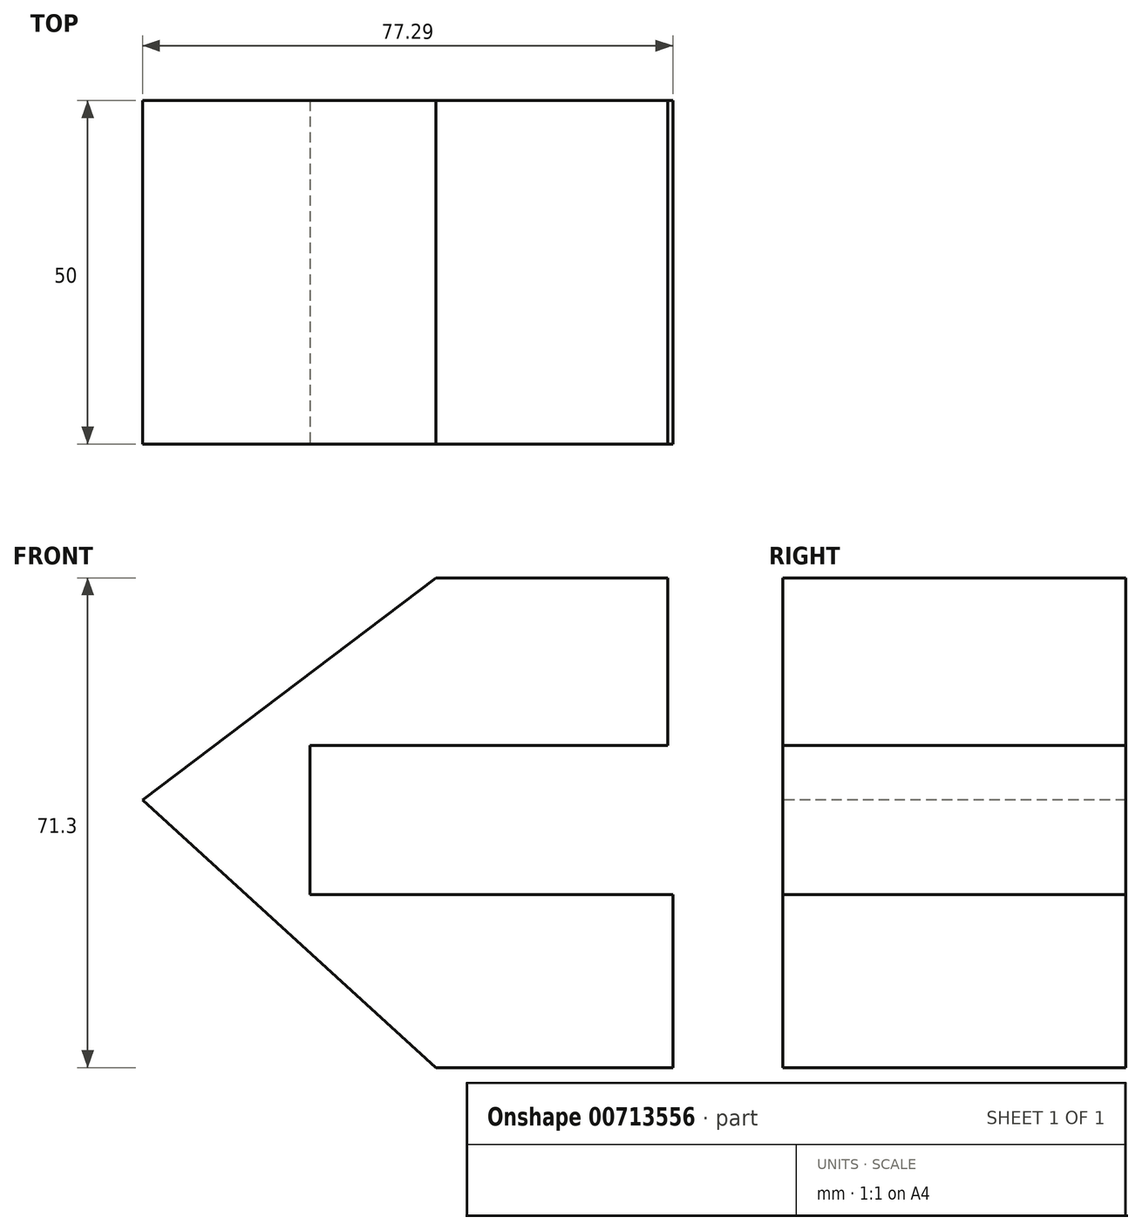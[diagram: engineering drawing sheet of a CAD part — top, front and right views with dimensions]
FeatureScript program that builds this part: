
annotation { "Feature Type Name" : "Feature", "Feature Type Description" : "" }
export const myFeature = defineFeature(function(context is Context, id is Id, definition is map)
    precondition{}
    {
        {
            var Q0;
            Q0=qCreatedBy(makeId("Front.planeOp"),FACE);
            var sketch = newSketch(context, id + "F0", { "sketchPlane" : qUnion([Q0])});
            skLineSegment(sketch, "E0", {"start": v(0, 0) * mm, "end": v(34.52, 0) * mm});
            skLineSegment(sketch, "E1", {"start": v(34.52, 0) * mm, "end": v(34.52, 25.21) * mm});
            skLineSegment(sketch, "E2", {"start": v(34.52, 25.21) * mm, "end": v(-18.35, 25.21) * mm});
            skLineSegment(sketch, "E3", {"start": v(-18.35, 25.21) * mm, "end": v(-18.35, 46.9) * mm});
            skLineSegment(sketch, "E4", {"start": v(-18.35, 46.9) * mm, "end": v(33.77, 46.9) * mm});
            skLineSegment(sketch, "E5", {"start": v(33.77, 46.9) * mm, "end": v(33.77, 71.3) * mm});
            skLineSegment(sketch, "E6", {"start": v(33.77, 71.3) * mm, "end": v(0, 71.3) * mm});
            skLineSegment(sketch, "E7", {"start": v(0, 71.3) * mm, "end": v(-42.77, 38.93) * mm});
            skLineSegment(sketch, "E8", {"start": v(-42.77, 38.93) * mm, "end": v(0, 0) * mm});
            skSolve(sketch);
        }
        {
            var Q0;
            Q0=makeQuery(id+"F0.imprint","IMPRINT",FACE,{"disambiguationData":[TD([[makeQuery(id+"F0.imprint","IMPRINT",EDGE,{"derivedFrom":sQuery(id+"F0.wireOp",EDGE,"E0")}),1.0]])]});
            extrude(context, id + "F1", {"entities" : qUnion([Q0]), "oppositeDirection" : true, "depth" : 25 * mm, "offsetDistance" : 25 * mm, "hasSecondDirection" : true, "secondDirectionOppositeDirection" : false, "secondDirectionDepth" : 25 * mm});
        }
    });
